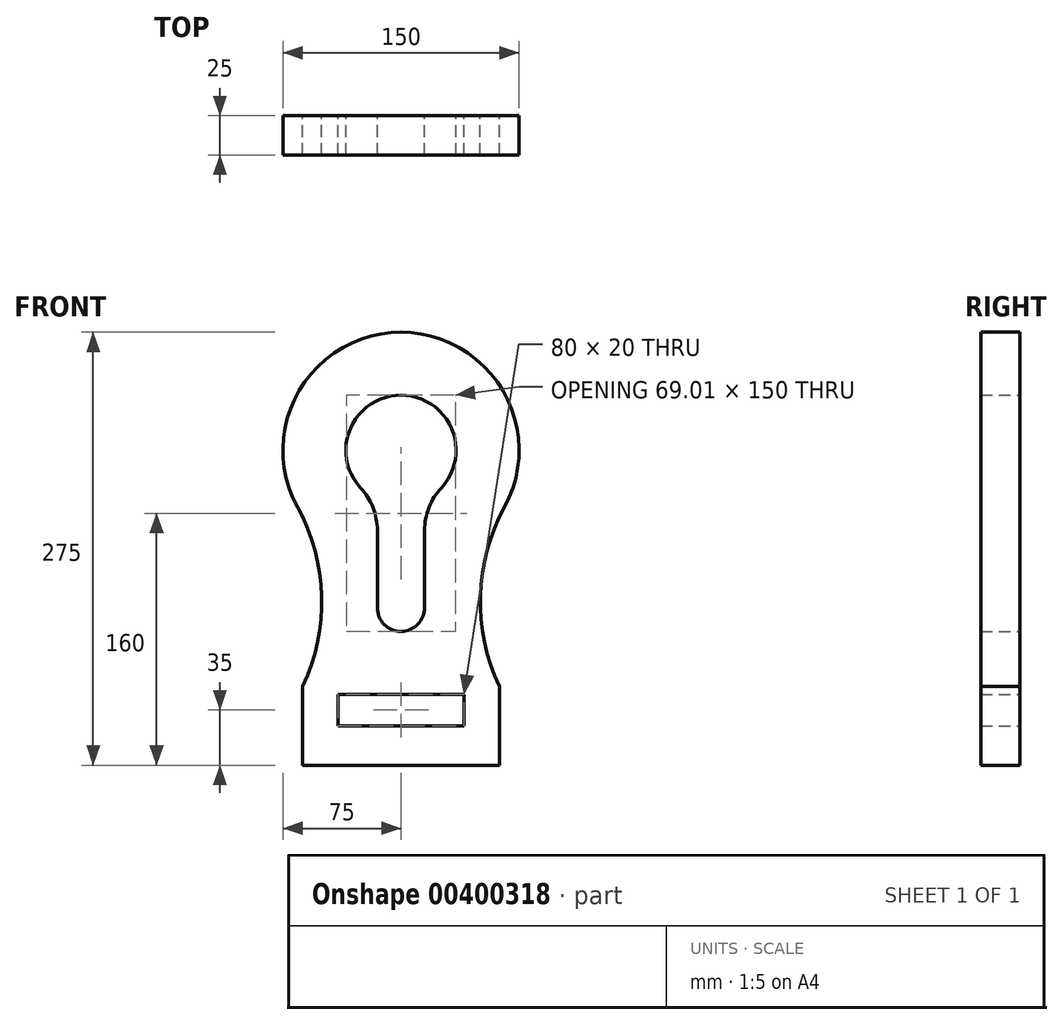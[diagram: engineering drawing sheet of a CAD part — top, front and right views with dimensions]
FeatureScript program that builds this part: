
annotation { "Feature Type Name" : "Feature", "Feature Type Description" : "" }
export const myFeature = defineFeature(function(context is Context, id is Id, definition is map)
    precondition{}
    {
        {
            var Q0;
            Q0=qCreatedBy(makeId("Front.planeOp"),FACE);
            var sketch = newSketch(context, id + "F0", { "sketchPlane" : qUnion([Q0])});
            skLineSegment(sketch, "E0", {"start": v(0, 0) * mm, "end": v(-62.5, 0) * mm});
            skLineSegment(sketch, "E1", {"start": v(-62.5, 0) * mm, "end": v(-62.5, 50) * mm});
            skLineSegment(sketch, "E2", {"start": v(0, 0) * mm, "end": v(0, 100) * mm, "construction": true});
            skArc(sketch, "E3", {"start": v(65.75, 163.92) * mm, "mid": v(0, 275) * mm, "end": v(-65.75, 163.92) * mm});
            skArc(sketch, "E4", {"start": v(-62.5, 50) * mm, "mid": v(-50.39, 107.35) * mm, "end": v(-65.75, 163.92) * mm});
            skArc(sketch, "E5.MirrorCS", {"start": v(62.5, 50) * mm, "mid": v(50.39, 107.35) * mm, "end": v(65.75, 163.92) * mm});
            skLineSegment(sketch, "E6.MirrorCS", {"start": v(62.5, 0) * mm, "end": v(62.5, 50) * mm});
            skLineSegment(sketch, "E7.MirrorCS", {"start": v(0, 0) * mm, "end": v(62.5, 0) * mm});
            skArc(sketch, "E8.0", {"start": v(25.67, 176.2) * mm, "mid": v(0, 235) * mm, "end": v(-25.67, 176.2) * mm});
            skLineSegment(sketch, "E9", {"start": v(-15, 100) * mm, "end": v(-15, 149) * mm});
            skLineSegment(sketch, "E10.MirrorCS", {"start": v(15, 100) * mm, "end": v(15, 149) * mm});
            skArc(sketch, "E11", {"start": v(-15, 100) * mm, "mid": v(0, 85) * mm, "end": v(15, 100) * mm});
            skArc(sketch, "E12", {"start": v(-15, 149) * mm, "mid": v(-17.76, 163.62) * mm, "end": v(-25.67, 176.2) * mm});
            skPoint(sketch, "E13.orphan", {"position": v(-15, 183.02) * mm});
            skArc(sketch, "E14.MirrorCS", {"start": v(15, 149) * mm, "mid": v(17.76, 163.62) * mm, "end": v(25.67, 176.2) * mm});
            skPoint(sketch, "E15.orphan", {"position": v(15, 183.02) * mm});
            skLineSegment(sketch, "E16.bottom", {"start": v(40, 45) * mm, "end": v(-40, 45) * mm});
            skLineSegment(sketch, "E16.top", {"start": v(40, 25) * mm, "end": v(-40, 25) * mm});
            skLineSegment(sketch, "E16.left", {"start": v(40, 45) * mm, "end": v(40, 25) * mm});
            skLineSegment(sketch, "E16.right", {"start": v(-40, 45) * mm, "end": v(-40, 25) * mm});
            skPoint(sketch, "E16.middle", {"position": v(0, 35) * mm});
            skSolve(sketch);
        }
        {
            var Q0;
            Q0=makeQuery(id+"F0.imprint","IMPRINT",FACE,{"disambiguationData":[TD([[makeQuery(id+"F0.imprint","IMPRINT",EDGE,{"derivedFrom":sQuery(id+"F0.wireOp",EDGE,"E0")}),-1.0]])]});
            extrude(context, id + "F1", {"entities" : qUnion([Q0]), "depth" : 25 * mm, "offsetDistance" : 25 * mm});
        }
    });
